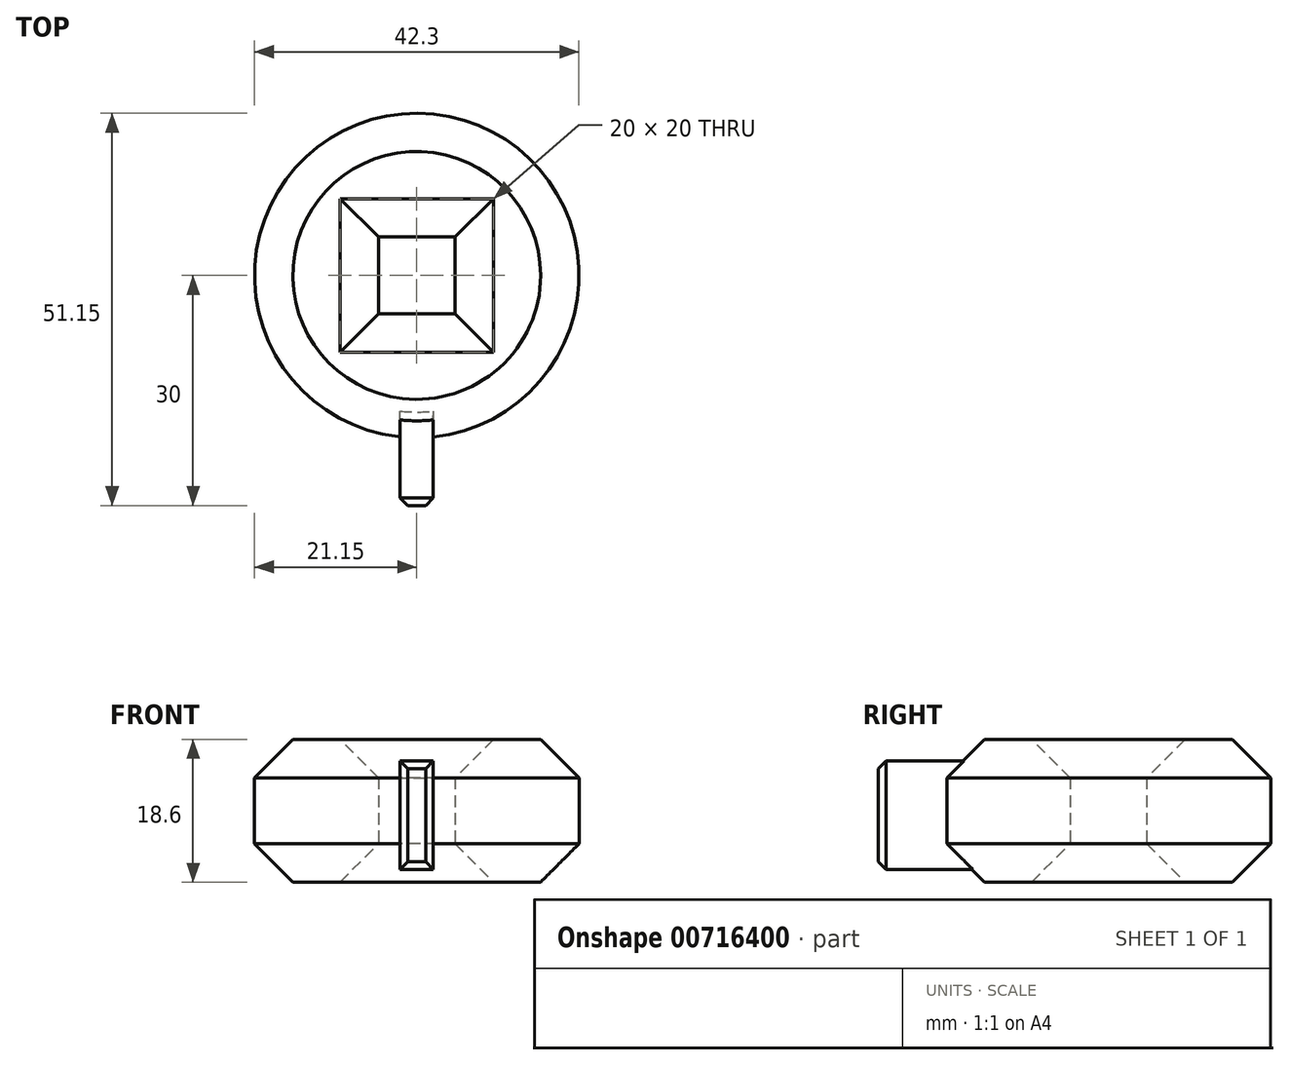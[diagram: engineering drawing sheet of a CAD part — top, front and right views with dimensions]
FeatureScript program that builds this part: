
annotation { "Feature Type Name" : "Feature", "Feature Type Description" : "" }
export const myFeature = defineFeature(function(context is Context, id is Id, definition is map)
    precondition{}
    {
        {
            var Q0;
            Q0=qCreatedBy(makeId("Top.planeOp"),FACE);
            var sketch = newSketch(context, id + "F0", { "sketchPlane" : qUnion([Q0])});
            skCircle(sketch, "E0", {"center": v(0, 0) * mm, "radius": 21.15 * mm});
            skLineSegment(sketch, "E1.bottom", {"start": v(5, -5) * mm, "end": v(-5, -5) * mm});
            skLineSegment(sketch, "E1.top", {"start": v(5, 5) * mm, "end": v(-5, 5) * mm});
            skLineSegment(sketch, "E1.left", {"start": v(5, -5) * mm, "end": v(5, 5) * mm});
            skLineSegment(sketch, "E1.right", {"start": v(-5, -5) * mm, "end": v(-5, 5) * mm});
            skSolve(sketch);
        }
        {
            var Q0;
            Q0=makeQuery(id+"F0.imprint","IMPRINT",FACE,{"disambiguationData":[TD([[makeQuery(id+"F0.imprint","IMPRINT",EDGE,{"derivedFrom":sQuery(id+"F0.wireOp",EDGE,"E0")}),1.0]])]});
            extrude(context, id + "F1", {"entities" : qUnion([Q0]), "depth" : 18.6 * mm, "offsetDistance" : 25 * mm});
        }
        {
            var Q0;
            Q0=qCreatedBy(makeId("Front.planeOp"),FACE);
            cPlane(context, id + "F2", {"entities" : qUnion([Q0]), "cplaneType" : CPlaneType.OFFSET, "offset" : 20 * mm, "width" : 150 * mm, "height" : 150 * mm});
        }
        {
            var Q0;
            Q0=qCreatedBy(id+"F2.planeOp",FACE);
            var sketch = newSketch(context, id + "F3", { "sketchPlane" : qUnion([Q0])});
            skLineSegment(sketch, "E2.bottom", {"start": v(2.16, 15.8) * mm, "end": v(-2.16, 15.8) * mm});
            skLineSegment(sketch, "E2.top", {"start": v(2.16, 1.66) * mm, "end": v(-2.16, 1.66) * mm});
            skLineSegment(sketch, "E2.left", {"start": v(2.16, 15.8) * mm, "end": v(2.16, 1.66) * mm});
            skLineSegment(sketch, "E2.right", {"start": v(-2.16, 15.8) * mm, "end": v(-2.16, 1.66) * mm});
            skPoint(sketch, "E2.middle", {"position": v(0, 8.73) * mm});
            skSolve(sketch);
        }
        {
            var Q0;
            Q0 = qSketchRegion(id + "F3", true);
            extrude(context, id + "F4", {"entities" : qUnion([Q0]), "operationType" : NewBodyOperationType.ADD, "depth" : 10 * mm, "offsetDistance" : 25 * mm, "hasSecondDirection" : true, "secondDirectionOppositeDirection" : true, "secondDirectionDepth" : 3.9 * mm});
        }
        {
            var Q0;
            Q0=makeQuery(id+"F1.opExtrude","CAP_EDGE",EDGE,{"disambiguationData":[OSD([sQuery(id+"F0.wireOp",EDGE,"E1.left")])],"isStart":false});
            var Q1;
            Q1=makeQuery(id+"F1.opExtrude","CAP_EDGE",EDGE,{"disambiguationData":[OSD([sQuery(id+"F0.wireOp",EDGE,"E1.top")])],"isStart":false});
            var Q2;
            Q2=makeQuery(id+"F1.opExtrude","CAP_EDGE",EDGE,{"disambiguationData":[OSD([sQuery(id+"F0.wireOp",EDGE,"E1.right")])],"isStart":false});
            var Q3;
            Q3=makeQuery(id+"F1.opExtrude","CAP_EDGE",EDGE,{"disambiguationData":[OSD([sQuery(id+"F0.wireOp",EDGE,"E1.bottom")])],"isStart":false});
            var Q4;
            Q4=makeQuery(id+"F1.opExtrude","CAP_FACE",FACE,{"disambiguationData":[OSD([sQuery(id+"F0.wireOp",EDGE,"E0"),sQuery(id+"F0.wireOp",EDGE,"E1.bottom"),sQuery(id+"F0.wireOp",EDGE,"E1.top"),sQuery(id+"F0.wireOp",EDGE,"E1.left"),sQuery(id+"F0.wireOp",EDGE,"E1.right")])],"isStart":false});
            var Q5;
            Q5=makeQuery(id+"F1.opExtrude","CAP_FACE",FACE,{"disambiguationData":[OSD([sQuery(id+"F0.wireOp",EDGE,"E0"),sQuery(id+"F0.wireOp",EDGE,"E1.bottom"),sQuery(id+"F0.wireOp",EDGE,"E1.top"),sQuery(id+"F0.wireOp",EDGE,"E1.left"),sQuery(id+"F0.wireOp",EDGE,"E1.right")])],"isStart":true});
            chamfer(context, id + "F5", {"entities" : qUnion([Q0, Q1, Q2, Q3, Q4, Q5]), "width" : 5 * mm, "tangentPropagation" : true});
        }
        {
            var Q0;
            Q0=makeQuery(id+"F4.opExtrude","CAP_FACE",FACE,{"disambiguationData":[OSD([sQuery(id+"F3.wireOp",EDGE,"E2.bottom"),sQuery(id+"F3.wireOp",EDGE,"E2.top"),sQuery(id+"F3.wireOp",EDGE,"E2.left"),sQuery(id+"F3.wireOp",EDGE,"E2.right")])],"isStart":false});
            var Q1;
            Q1=makeQuery(id+"FGEJDNJx6kN0rpz_1.7.F4.opExtrude","CAP_FACE",FACE,{"disambiguationData":[OSD([sQuery(id+"F3.wireOp",EDGE,"E2.bottom"),sQuery(id+"F3.wireOp",EDGE,"E2.top"),sQuery(id+"F3.wireOp",EDGE,"E2.left"),sQuery(id+"F3.wireOp",EDGE,"E2.right")])],"isStart":false});
            var Q2;
            Q2=makeQuery(id+"FGEJDNJx6kN0rpz_1.6.F4.opExtrude","CAP_FACE",FACE,{"disambiguationData":[OSD([sQuery(id+"F3.wireOp",EDGE,"E2.bottom"),sQuery(id+"F3.wireOp",EDGE,"E2.top"),sQuery(id+"F3.wireOp",EDGE,"E2.left"),sQuery(id+"F3.wireOp",EDGE,"E2.right")])],"isStart":false});
            var Q3;
            Q3=makeQuery(id+"FGEJDNJx6kN0rpz_1.5.F4.opExtrude","CAP_FACE",FACE,{"disambiguationData":[OSD([sQuery(id+"F3.wireOp",EDGE,"E2.bottom"),sQuery(id+"F3.wireOp",EDGE,"E2.top"),sQuery(id+"F3.wireOp",EDGE,"E2.left"),sQuery(id+"F3.wireOp",EDGE,"E2.right")])],"isStart":false});
            var Q4;
            Q4=makeQuery(id+"FGEJDNJx6kN0rpz_1.4.F4.opExtrude","CAP_FACE",FACE,{"disambiguationData":[OSD([sQuery(id+"F3.wireOp",EDGE,"E2.bottom"),sQuery(id+"F3.wireOp",EDGE,"E2.top"),sQuery(id+"F3.wireOp",EDGE,"E2.left"),sQuery(id+"F3.wireOp",EDGE,"E2.right")])],"isStart":false});
            var Q5;
            Q5=makeQuery(id+"FGEJDNJx6kN0rpz_1.3.F4.opExtrude","CAP_FACE",FACE,{"disambiguationData":[OSD([sQuery(id+"F3.wireOp",EDGE,"E2.bottom"),sQuery(id+"F3.wireOp",EDGE,"E2.top"),sQuery(id+"F3.wireOp",EDGE,"E2.left"),sQuery(id+"F3.wireOp",EDGE,"E2.right")])],"isStart":false});
            var Q6;
            Q6=makeQuery(id+"FGEJDNJx6kN0rpz_1.2.F4.opExtrude","CAP_FACE",FACE,{"disambiguationData":[OSD([sQuery(id+"F3.wireOp",EDGE,"E2.bottom"),sQuery(id+"F3.wireOp",EDGE,"E2.top"),sQuery(id+"F3.wireOp",EDGE,"E2.left"),sQuery(id+"F3.wireOp",EDGE,"E2.right")])],"isStart":false});
            var Q7;
            Q7=makeQuery(id+"FGEJDNJx6kN0rpz_1.1.F4.opExtrude","CAP_EDGE",EDGE,{"disambiguationData":[OSD([sQuery(id+"F3.wireOp",EDGE,"E2.right")])],"isStart":false});
            chamfer(context, id + "F6", {"entities" : qUnion([Q0, Q1, Q2, Q3, Q4, Q5, Q6, Q7]), "width" : 1 * mm, "tangentPropagation" : true});
        }
    });
